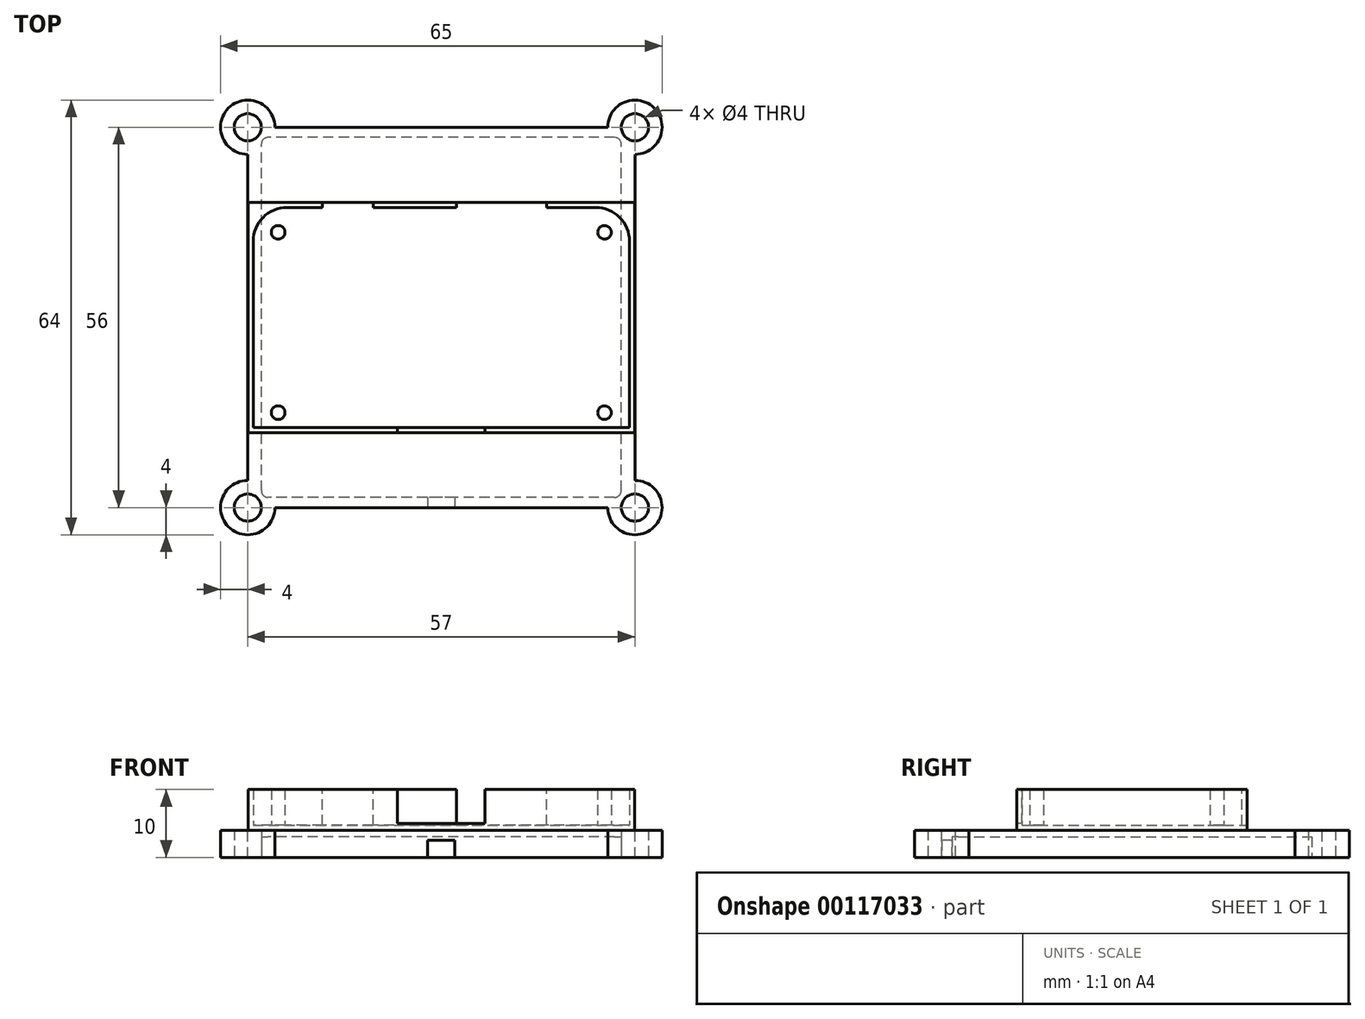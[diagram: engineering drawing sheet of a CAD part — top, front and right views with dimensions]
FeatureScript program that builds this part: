
annotation { "Feature Type Name" : "Feature", "Feature Type Description" : "" }
export const myFeature = defineFeature(function(context is Context, id is Id, definition is map)
    precondition{}
    {
        {
            var Q0;
            Q0=qCreatedBy(makeId("Top.planeOp"),FACE);
            var sketch = newSketch(context, id + "F0", { "sketchPlane" : qUnion([Q0])});
            skLineSegment(sketch, "E0.bottom", {"start": v(21.52, 16.02) * mm, "end": v(-21.53, 16.02) * mm, "construction": true});
            skLineSegment(sketch, "E0.top", {"start": v(27.53, -16.02) * mm, "end": v(-27.53, -16.02) * mm, "construction": true});
            skLineSegment(sketch, "E0.left", {"start": v(27.53, 10.02) * mm, "end": v(27.53, -16.02) * mm, "construction": true});
            skLineSegment(sketch, "E0.right", {"start": v(-27.53, 10.02) * mm, "end": v(-27.53, -16.02) * mm, "construction": true});
            skPoint(sketch, "E0.middle", {"position": v(0, 0) * mm});
            skLineSegment(sketch, "E1", {"start": v(15.52, 16.02) * mm, "end": v(15.52, 20.98) * mm, "construction": true});
            skLineSegment(sketch, "E2", {"start": v(15.52, 20.98) * mm, "end": v(2.27, 20.98) * mm, "construction": true});
            skLineSegment(sketch, "E3", {"start": v(2.27, 20.98) * mm, "end": v(2.27, 16.02) * mm, "construction": true});
            skLineSegment(sketch, "E4", {"start": v(-10.03, 16.02) * mm, "end": v(-10.03, 20.58) * mm, "construction": true});
            skLineSegment(sketch, "E5", {"start": v(-10.02, 20.58) * mm, "end": v(-17.52, 20.58) * mm, "construction": true});
            skLineSegment(sketch, "E6", {"start": v(-17.53, 20.58) * mm, "end": v(-17.53, 16.02) * mm, "construction": true});
            skCircle(sketch, "E7", {"center": v(24.02, 12.52) * mm, "radius": 1.5 * mm, "construction": true});
            skCircle(sketch, "E8", {"center": v(-24.03, 12.52) * mm, "radius": 1.5 * mm, "construction": true});
            skPoint(sketch, "E9.visualSharp", {"position": v(-27.53, 16.02) * mm});
            skArc(sketch, "E9.filletArc", {"start": v(-21.53, 16.02) * mm, "mid": v(-25.77, 14.27) * mm, "end": v(-27.53, 10.02) * mm, "construction": true});
            skPoint(sketch, "E10.visualSharp", {"position": v(27.53, 16.02) * mm});
            skArc(sketch, "E10.filletArc", {"start": v(27.53, 10.02) * mm, "mid": v(25.77, 14.27) * mm, "end": v(21.52, 16.02) * mm, "construction": true});
            skCircle(sketch, "E11", {"center": v(-24.03, -14.02) * mm, "radius": 1.5 * mm, "construction": true});
            skCircle(sketch, "E12", {"center": v(24.02, -14.02) * mm, "radius": 1.5 * mm, "construction": true});
            skSolve(sketch);
        }
        {
            var Q0;
            Q0=qCreatedBy(makeId("Top.planeOp"),FACE);
            var sketch = newSketch(context, id + "F1", { "sketchPlane" : qUnion([Q0])});
            skLineSegment(sketch, "E13", {"start": v(-28.45, -16.95) * mm, "end": v(-28.45, 16.95) * mm});
            skLineSegment(sketch, "E14", {"start": v(-28.45, -16.95) * mm, "end": v(28.45, -16.95) * mm});
            skLineSegment(sketch, "E15", {"start": v(28.45, -16.95) * mm, "end": v(28.45, 16.95) * mm});
            skLineSegment(sketch, "E16", {"start": v(28.45, 16.95) * mm, "end": v(16.2, 16.95) * mm});
            skLineSegment(sketch, "E17", {"start": v(16.2, 16.95) * mm, "end": v(1.45, 16.95) * mm});
            skLineSegment(sketch, "E18", {"start": v(1.45, 16.95) * mm, "end": v(-9.05, 16.95) * mm});
            skLineSegment(sketch, "E19", {"start": v(-9.05, 16.95) * mm, "end": v(-18.3, 16.95) * mm});
            skLineSegment(sketch, "E20", {"start": v(-18.3, 16.95) * mm, "end": v(-28.45, 16.95) * mm});
            skPoint(sketch, "E21", {"position": v(0, -16.95) * mm});
            skPoint(sketch, "E22", {"position": v(28.45, 0) * mm});
            skSolve(sketch);
        }
        {
            var Q0;
            Q0 = qSketchRegion(id + "F1", true);
            extrude(context, id + "F2", {"entities" : qUnion([Q0]), "depth" : 6 * mm});
        }
        {
            var Q0;
            Q0=makeQuery(id+"F2.opExtrude","CAP_FACE",FACE,{"disambiguationData":[OSD([sQuery(id+"F1.wireOp",EDGE,"E13"),sQuery(id+"F1.wireOp",EDGE,"E14"),sQuery(id+"F1.wireOp",EDGE,"E15"),sQuery(id+"F1.wireOp",EDGE,"E16"),sQuery(id+"F1.wireOp",EDGE,"E17"),sQuery(id+"F1.wireOp",EDGE,"E18"),sQuery(id+"F1.wireOp",EDGE,"E19"),sQuery(id+"F1.wireOp",EDGE,"E20")])],"isStart":false});
            shell(context, id + "F3", {"entities" : qUnion([Q0]), "thickness" : .75 * mm});
        }
        {
            var Q0;
            Q0=qCreatedBy(makeId("Top.planeOp"),FACE);
            var sketch = newSketch(context, id + "F4", { "sketchPlane" : qUnion([Q0])});
            skCircle(sketch, "E23", {"center": v(-24.03, 12.52) * mm, "radius": 1 * mm});
            skCircle(sketch, "E24", {"center": v(24.02, 12.52) * mm, "radius": 1 * mm});
            skCircle(sketch, "E25", {"center": v(-24.03, -14.02) * mm, "radius": 1 * mm});
            skCircle(sketch, "E26", {"center": v(24.02, -14.02) * mm, "radius": 1 * mm});
            skSolve(sketch);
        }
        {
            var Q0;
            Q0 = qSketchRegion(id + "F4", true);
            var Q1;
            Q1 = qConstructionFilter(qBodyType(qCreatedBy(id + "F4" ,EDGE), BodyType.WIRE), ConstructionObject.NO);
            extrude(context, id + "F5", {"entities" : qUnion([Q0]), "operationType" : NewBodyOperationType.ADD, "surfaceEntities" : qUnion([Q1]), "depth" : 6 * mm});
        }
        {
            var Q0;
            Q0=makeQuery(id+"F2.opExtrude","SWEPT_FACE",FACE,{"disambiguationData":[OSD([sQuery(id+"F1.wireOp",EDGE,"E16"),sQuery(id+"F1.wireOp",EDGE,"E17"),sQuery(id+"F1.wireOp",EDGE,"E18"),sQuery(id+"F1.wireOp",EDGE,"E19"),sQuery(id+"F1.wireOp",EDGE,"E20")])]});
            var sketch = newSketch(context, id + "F6", { "sketchPlane" : qUnion([Q0])});
            skLineSegment(sketch, "E27.top", {"start": v(-2.25, 6) * mm, "end": v(-15.5, 6) * mm});
            skLineSegment(sketch, "E27.left", {"start": v(-2.25, 0.75) * mm, "end": v(-2.25, 6) * mm});
            skLineSegment(sketch, "E27.right", {"start": v(-15.5, 0.75) * mm, "end": v(-15.5, 6) * mm});
            skLineSegment(sketch, "E28.top", {"start": v(10, 6) * mm, "end": v(17.5, 6) * mm});
            skLineSegment(sketch, "E28.left", {"start": v(10, 0.75) * mm, "end": v(10, 6) * mm});
            skLineSegment(sketch, "E28.right", {"start": v(17.5, 0.75) * mm, "end": v(17.5, 6) * mm});
            skLineSegment(sketch, "E29", {"start": v(-15.5, 0.75) * mm, "end": v(-2.25, 0.75) * mm});
            skLineSegment(sketch, "E30", {"start": v(10, 0.75) * mm, "end": v(17.5, 0.75) * mm});
            skSolve(sketch);
        }
        {
            var Q0;
            Q0 = qSketchRegion(id + "F6", true);
            extrude(context, id + "F7", {"entities" : qUnion([Q0]), "operationType" : NewBodyOperationType.REMOVE, "oppositeDirection" : true, "depth" : .75 * mm});
        }
        {
            var Q0;
            Q0=makeQuery(id+"F2.opExtrude","CAP_FACE",FACE,{"disambiguationData":[OSD([sQuery(id+"F1.wireOp",EDGE,"E13"),sQuery(id+"F1.wireOp",EDGE,"E14"),sQuery(id+"F1.wireOp",EDGE,"E15"),sQuery(id+"F1.wireOp",EDGE,"E16"),sQuery(id+"F1.wireOp",EDGE,"E17"),sQuery(id+"F1.wireOp",EDGE,"E18"),sQuery(id+"F1.wireOp",EDGE,"E19"),sQuery(id+"F1.wireOp",EDGE,"E20")])],"isStart":true});
            var sketch = newSketch(context, id + "F8", { "sketchPlane" : qUnion([Q0])});
            skLineSegment(sketch, "E31.bottom", {"start": v(26.25, -26.25) * mm, "end": v(-26.25, -26.25) * mm, "construction": true});
            skLineSegment(sketch, "E31.top", {"start": v(26.25, 26.25) * mm, "end": v(-26.25, 26.25) * mm, "construction": true});
            skLineSegment(sketch, "E31.left", {"start": v(26.25, -26.25) * mm, "end": v(26.25, 26.25) * mm, "construction": true});
            skLineSegment(sketch, "E31.right", {"start": v(-26.25, -26.25) * mm, "end": v(-26.25, 26.25) * mm, "construction": true});
            skPoint(sketch, "E31.middle", {"position": v(0, 0) * mm});
            skLineSegment(sketch, "E32.bottom", {"start": v(28.5, 28) * mm, "end": v(-28.5, 28) * mm});
            skLineSegment(sketch, "E32.top", {"start": v(28.5, -28) * mm, "end": v(-28.5, -28) * mm});
            skLineSegment(sketch, "E32.left", {"start": v(28.5, 28) * mm, "end": v(28.5, -28) * mm});
            skLineSegment(sketch, "E32.right", {"start": v(-28.5, 28) * mm, "end": v(-28.5, -28) * mm});
            skCircle(sketch, "E33", {"center": v(28.5, -28) * mm, "radius": 4 * mm});
            skCircle(sketch, "E34", {"center": v(28.5, 28) * mm, "radius": 4 * mm});
            skCircle(sketch, "E35", {"center": v(-28.5, 28) * mm, "radius": 4 * mm});
            skCircle(sketch, "E36", {"center": v(-28.5, -28) * mm, "radius": 4 * mm});
            skSolve(sketch);
        }
        {
            var Q0;
            Q0 = qSketchRegion(id + "F8", true);
            extrude(context, id + "F9", {"entities" : qUnion([Q0]), "operationType" : NewBodyOperationType.ADD, "depth" : 4 * mm});
        }
        {
            var Q0;
            Q0=makeQuery(id+"F2.opExtrude","SWEPT_FACE",FACE,{"disambiguationData":[OSD([sQuery(id+"F1.wireOp",EDGE,"E14")])]});
            var sketch = newSketch(context, id + "F10", { "sketchPlane" : qUnion([Q0])});
            skLineSegment(sketch, "E37.bottom", {"start": v(-6.45, 6) * mm, "end": v(6.45, 6) * mm});
            skLineSegment(sketch, "E37.left", {"start": v(-6.45, 6) * mm, "end": v(-6.45, 1) * mm});
            skLineSegment(sketch, "E37.right", {"start": v(6.45, 6) * mm, "end": v(6.45, 1) * mm});
            skLineSegment(sketch, "E38", {"start": v(-6.45, 1) * mm, "end": v(6.45, 1) * mm});
            skSolve(sketch);
        }
        {
            var Q0;
            Q0=makeQuery(id+"F10.imprint","IMPRINT",FACE,{"disambiguationData":[TD([[makeQuery(id+"F10.imprint","IMPRINT",EDGE,{"derivedFrom":sQuery(id+"F10.wireOp",EDGE,"E37.bottom")}),-1.0]])]});
            extrude(context, id + "F11", {"entities" : qUnion([Q0]), "operationType" : NewBodyOperationType.REMOVE, "oppositeDirection" : true, "depth" : 1 * mm});
        }
        {
            var Q0;
            Q0=makeQuery(id+"F9.opExtrude","CAP_FACE",FACE,{"disambiguationData":[OSD([sQuery(id+"F8.wireOp",EDGE,"E32.bottom"),sQuery(id+"F8.wireOp",EDGE,"E32.top"),sQuery(id+"F8.wireOp",EDGE,"E32.left"),sQuery(id+"F8.wireOp",EDGE,"E32.right"),sQuery(id+"F8.wireOp",EDGE,"E33"),sQuery(id+"F8.wireOp",EDGE,"E34"),sQuery(id+"F8.wireOp",EDGE,"E35"),sQuery(id+"F8.wireOp",EDGE,"E36")])],"isStart":false});
            var sketch = newSketch(context, id + "F12", { "sketchPlane" : qUnion([Q0])});
            skCircle(sketch, "E39", {"center": v(-28.5, 28) * mm, "radius": 2 * mm});
            skCircle(sketch, "E40", {"center": v(28.5, 28) * mm, "radius": 2 * mm});
            skCircle(sketch, "E41", {"center": v(28.5, -28) * mm, "radius": 2 * mm});
            skCircle(sketch, "E42", {"center": v(-28.5, -28) * mm, "radius": 2 * mm});
            skSolve(sketch);
        }
        {
            var Q0;
            Q0 = qSketchRegion(id + "F12", true);
            extrude(context, id + "F13", {"entities" : qUnion([Q0]), "operationType" : NewBodyOperationType.REMOVE, "endBound" : BoundingType.UP_TO_NEXT, "oppositeDirection" : true, "depth" : 25 * mm});
        }
        {
            var Q0;
            Q0=makeQuery(id+"F9.opExtrude","CAP_FACE",FACE,{"disambiguationData":[OSD([sQuery(id+"F8.wireOp",EDGE,"E32.bottom"),sQuery(id+"F8.wireOp",EDGE,"E32.top"),sQuery(id+"F8.wireOp",EDGE,"E32.left"),sQuery(id+"F8.wireOp",EDGE,"E32.right"),sQuery(id+"F8.wireOp",EDGE,"E33"),sQuery(id+"F8.wireOp",EDGE,"E34"),sQuery(id+"F8.wireOp",EDGE,"E35"),sQuery(id+"F8.wireOp",EDGE,"E36")])],"isStart":false});
            var sketch = newSketch(context, id + "F14", { "sketchPlane" : qUnion([Q0])});
            skLineSegment(sketch, "E43.bottom", {"start": v(26.5, 26.5) * mm, "end": v(-26.5, 26.5) * mm});
            skLineSegment(sketch, "E43.top", {"start": v(26.5, -26.5) * mm, "end": v(-26.5, -26.5) * mm});
            skLineSegment(sketch, "E43.left", {"start": v(26.5, 26.5) * mm, "end": v(26.5, -26.5) * mm});
            skLineSegment(sketch, "E43.right", {"start": v(-26.5, 26.5) * mm, "end": v(-26.5, -26.5) * mm});
            skPoint(sketch, "E43.middle", {"position": v(0, 0) * mm});
            skSolve(sketch);
        }
        {
            var Q0;
            Q0 = qSketchRegion(id + "F14", true);
            extrude(context, id + "F15", {"entities" : qUnion([Q0]), "operationType" : NewBodyOperationType.REMOVE, "oppositeDirection" : true, "depth" : 3 * mm});
        }
        {
            var Q0;
            Q0=makeQuery(id+"F15.boolean.opBoolean","COPY",EDGE,{"derivedFrom":makeQuery(id+"F15.opExtrude","SWEPT_EDGE",EDGE,{"disambiguationData":[OSD([sQuery(id+"F14.wireOp",EDGE,"E43.bottom"),sQuery(id+"F14.wireOp",EDGE,"E43.right")])]})});
            var Q1;
            Q1=makeQuery(id+"F15.boolean.opBoolean","COPY",EDGE,{"derivedFrom":makeQuery(id+"F15.opExtrude","SWEPT_EDGE",EDGE,{"disambiguationData":[OSD([sQuery(id+"F14.wireOp",EDGE,"E43.bottom"),sQuery(id+"F14.wireOp",EDGE,"E43.left")])]})});
            var Q2;
            Q2=makeQuery(id+"F15.boolean.opBoolean","COPY",EDGE,{"derivedFrom":makeQuery(id+"F15.opExtrude","SWEPT_EDGE",EDGE,{"disambiguationData":[OSD([sQuery(id+"F14.wireOp",EDGE,"E43.top"),sQuery(id+"F14.wireOp",EDGE,"E43.left")])]})});
            var Q3;
            Q3=makeQuery(id+"F15.boolean.opBoolean","COPY",EDGE,{"derivedFrom":makeQuery(id+"F15.opExtrude","SWEPT_EDGE",EDGE,{"disambiguationData":[OSD([sQuery(id+"F14.wireOp",EDGE,"E43.top"),sQuery(id+"F14.wireOp",EDGE,"E43.right")])]})});
            fillet(context, id + "F16", {"entities" : qUnion([Q0, Q1, Q2, Q3]), "radius" : 1 * mm, "tangentPropagation" : true, "allowEdgeOverflow" : false});
        }
        {
            var Q0;
            Q0=makeQuery(id+"F3.opShell","OFFSET_EDGE",EDGE,{"disambiguationData":[OSD([sQuery(id+"F1.wireOp",EDGE,"E13"),sQuery(id+"F1.wireOp",EDGE,"E20")])]});
            var Q1;
            Q1=makeQuery(id+"F3.opShell","OFFSET_EDGE",EDGE,{"disambiguationData":[OSD([sQuery(id+"F1.wireOp",EDGE,"E15"),sQuery(id+"F1.wireOp",EDGE,"E16")])]});
            fillet(context, id + "F17", {"entities" : qUnion([Q0, Q1]), "radius" : 5 * mm, "tangentPropagation" : true, "allowEdgeOverflow" : false});
        }
        {
            var Q0;
            Q0=makeQuery(id+"F9.opExtrude","SWEPT_FACE",FACE,{"disambiguationData":[OSD([sQuery(id+"F8.wireOp",EDGE,"E32.bottom")])]});
            var sketch = newSketch(context, id + "F18", { "sketchPlane" : qUnion([Q0])});
            skLineSegment(sketch, "E44.bottom", {"start": v(-2, -1.5) * mm, "end": v(2, -1.5) * mm});
            skLineSegment(sketch, "E44.top", {"start": v(-2, -4) * mm, "end": v(2, -4) * mm});
            skLineSegment(sketch, "E44.left", {"start": v(-2, -1.5) * mm, "end": v(-2, -4) * mm});
            skLineSegment(sketch, "E44.right", {"start": v(2, -1.5) * mm, "end": v(2, -4) * mm});
            skPoint(sketch, "E45", {"position": v(0, -1.5) * mm});
            skSolve(sketch);
        }
        {
            var Q0;
            Q0=makeQuery(id+"F18.imprint","IMPRINT",FACE,{"disambiguationData":[TD([[makeQuery(id+"F18.imprint","IMPRINT",EDGE,{"derivedFrom":sQuery(id+"F18.wireOp",EDGE,"E44.bottom")}),-1.0]])]});
            extrude(context, id + "F19", {"entities" : qUnion([Q0]), "operationType" : NewBodyOperationType.REMOVE, "endBound" : BoundingType.UP_TO_NEXT, "oppositeDirection" : true, "depth" : 25 * mm});
        }
    });
